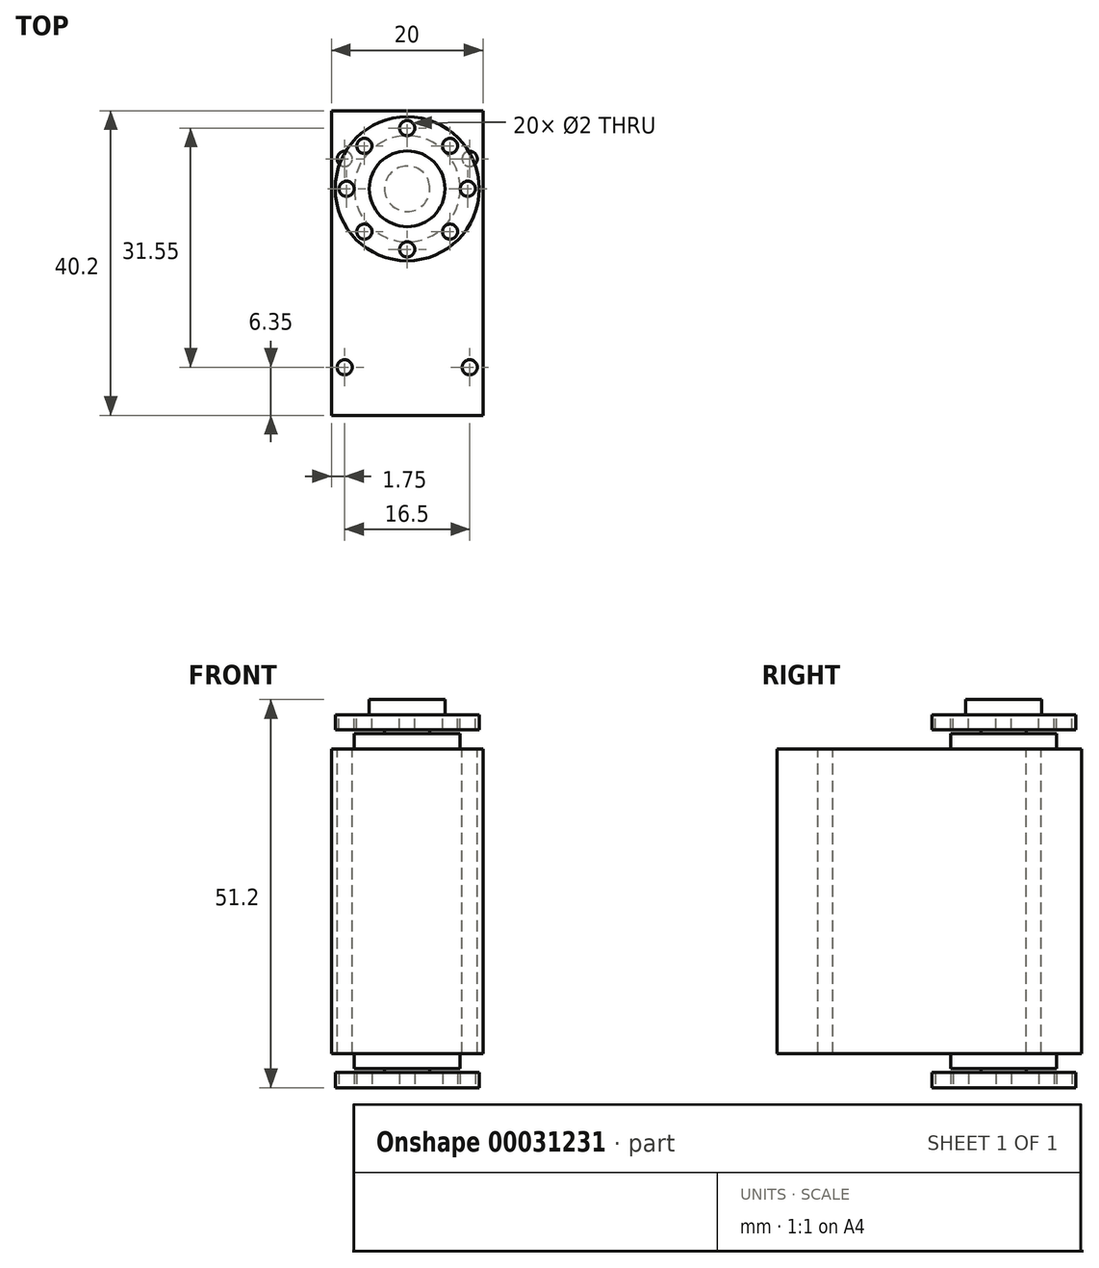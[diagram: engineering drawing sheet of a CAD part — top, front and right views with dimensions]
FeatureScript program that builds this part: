
annotation { "Feature Type Name" : "Feature", "Feature Type Description" : "" }
export const myFeature = defineFeature(function(context is Context, id is Id, definition is map)
    precondition{}
    {
        {
            var Q0;
            Q0=qCreatedBy(makeId("Top.planeOp"),FACE);
            var sketch = newSketch(context, id + "F0", { "sketchPlane" : qUnion([Q0])});
            skLineSegment(sketch, "E0.bottom", {"start": v(0, 0) * mm, "end": v(20, 0) * mm});
            skLineSegment(sketch, "E0.top", {"start": v(0, 40.2) * mm, "end": v(20, 40.2) * mm});
            skLineSegment(sketch, "E0.left", {"start": v(0, 0) * mm, "end": v(0, 40.2) * mm});
            skLineSegment(sketch, "E0.right", {"start": v(20, 0) * mm, "end": v(20, 40.2) * mm});
            skSolve(sketch);
        }
        {
            var Q0;
            Q0 = qSketchRegion(id + "F0", true);
            extrude(context, id + "F1", {"entities" : qUnion([Q0]), "depth" : 40.2 * mm});
        }
        {
            var Q0;
            Q0=makeQuery(id+"F1.opExtrude","CAP_FACE",FACE,{"disambiguationData":[OSD([sQuery(id+"F0.wireOp",EDGE,"E0.bottom"),sQuery(id+"F0.wireOp",EDGE,"E0.top"),sQuery(id+"F0.wireOp",EDGE,"E0.left"),sQuery(id+"F0.wireOp",EDGE,"E0.right")])],"isStart":false});
            var sketch = newSketch(context, id + "F2", { "sketchPlane" : qUnion([Q0])});
            skLineSegment(sketch, "E1", {"start": v(10, 40.2) * mm, "end": v(10, 0) * mm, "construction": true});
            skLineSegment(sketch, "E2", {"start": v(0, 20.1) * mm, "end": v(20, 20.1) * mm, "construction": true});
            skCircle(sketch, "E3", {"center": v(1.75, 33.85) * mm, "radius": 1 * mm});
            skCircle(sketch, "E4.MirrorC", {"center": v(18.25, 33.85) * mm, "radius": 1 * mm});
            skCircle(sketch, "E5.MirrorC", {"center": v(1.75, 6.35) * mm, "radius": 1 * mm});
            skCircle(sketch, "E6.MirrorC", {"center": v(18.25, 6.35) * mm, "radius": 1 * mm});
            skSolve(sketch);
        }
        {
            var Q0;
            Q0 = qSketchRegion(id + "F2", true);
            extrude(context, id + "F3", {"entities" : qUnion([Q0]), "operationType" : NewBodyOperationType.REMOVE, "endBound" : BoundingType.THROUGH_ALL, "oppositeDirection" : true, "depth" : 25 * mm});
        }
        {
            var Q0;
            Q0=makeQuery(id+"F1.opExtrude","CAP_FACE",FACE,{"disambiguationData":[OSD([sQuery(id+"F0.wireOp",EDGE,"E0.bottom"),sQuery(id+"F0.wireOp",EDGE,"E0.top"),sQuery(id+"F0.wireOp",EDGE,"E0.left"),sQuery(id+"F0.wireOp",EDGE,"E0.right")])],"isStart":false});
            var sketch = newSketch(context, id + "F4", { "sketchPlane" : qUnion([Q0])});
            skCircle(sketch, "E7", {"center": v(10, 29.9) * mm, "radius": 7 * mm});
            skLineSegment(sketch, "E8", {"start": v(0, 20.1) * mm, "end": v(20, 20.1) * mm, "construction": true});
            skSolve(sketch);
        }
        {
            var Q0;
            Q0 = qSketchRegion(id + "F4", true);
            extrude(context, id + "F5", {"entities" : qUnion([Q0]), "operationType" : NewBodyOperationType.ADD, "depth" : 2 * mm, "hasSecondDirection" : true, "secondDirectionOppositeDirection" : true, "secondDirectionDepth" : (40.2 + 2) * mm});
        }
        {
            var Q0;
            Q0=makeQuery(id+"F5.opExtrude","CAP_FACE",FACE,{"disambiguationData":[OSD([sQuery(id+"F4.wireOp",EDGE,"E7")])],"isStart":false});
            var sketch = newSketch(context, id + "F6", { "sketchPlane" : qUnion([Q0])});
            skCircle(sketch, "E9", {"center": v(10, 29.9) * mm, "radius": 3 * mm});
            skSolve(sketch);
        }
        {
            var Q0;
            Q0 = qSketchRegion(id + "F6", true);
            extrude(context, id + "F7", {"entities" : qUnion([Q0]), "operationType" : NewBodyOperationType.ADD, "depth" : 2.5 * mm});
        }
        {
            var Q0;
            Q0=makeQuery(id+"F7.opExtrude","CAP_FACE",FACE,{"disambiguationData":[OSD([sQuery(id+"F6.wireOp",EDGE,"E9")])],"isStart":false});
            var sketch = newSketch(context, id + "F8", { "sketchPlane" : qUnion([Q0])});
            skCircle(sketch, "E10", {"center": v(10, 29.9) * mm, "radius": 9.5 * mm});
            skCircle(sketch, "E11", {"center": v(10, 29.9) * mm, "radius": 8 * mm, "construction": true});
            skCircle(sketch, "E12", {"center": v(10, 37.9) * mm, "radius": 1 * mm});
            skCircle(sketch, "E13.1.0", {"center": v(4.34, 35.56) * mm, "radius": 1 * mm});
            skCircle(sketch, "E13.2.0", {"center": v(2, 29.9) * mm, "radius": 1 * mm});
            skCircle(sketch, "E13.3.0", {"center": v(4.34, 24.24) * mm, "radius": 1 * mm});
            skCircle(sketch, "E13.4.0", {"center": v(10, 21.9) * mm, "radius": 1 * mm});
            skCircle(sketch, "E13.5.0", {"center": v(15.66, 24.24) * mm, "radius": 1 * mm});
            skCircle(sketch, "E13.6.0", {"center": v(18, 29.9) * mm, "radius": 1 * mm});
            skCircle(sketch, "E13.7.0", {"center": v(15.66, 35.56) * mm, "radius": 1 * mm});
            skSolve(sketch);
        }
        {
            var Q0;
            Q0 = qSketchRegion(id + "F8", true);
            extrude(context, id + "F9", {"entities" : qUnion([Q0]), "operationType" : NewBodyOperationType.ADD, "oppositeDirection" : true, "depth" : 2 * mm});
        }
        {
            var Q0;
            Q0=qCreatedBy(makeId("Top.planeOp"),FACE);
            cPlane(context, id + "F10", {"entities" : qUnion([Q0]), "cplaneType" : CPlaneType.OFFSET, "offset" : (40.2 / 2) * mm, "width" : 150 * mm, "height" : 150 * mm});
        }
        {
            var Q0;
            Q0=makeQuery(id+"F9.opExtrude","SWEPT_BODY",BODY,{"disambiguationData":[OSD([sQuery(id+"F8.wireOp",EDGE,"E10"),sQuery(id+"F8.wireOp",EDGE,"E12"),sQuery(id+"F8.wireOp",EDGE,"E13.1.0"),sQuery(id+"F8.wireOp",EDGE,"E13.2.0"),sQuery(id+"F8.wireOp",EDGE,"E13.3.0"),sQuery(id+"F8.wireOp",EDGE,"E13.4.0"),sQuery(id+"F8.wireOp",EDGE,"E13.5.0"),sQuery(id+"F8.wireOp",EDGE,"E13.6.0"),sQuery(id+"F8.wireOp",EDGE,"E13.7.0")])]});
            var Q1;
            Q1=makeQuery(id+"F1.opExtrude","SWEPT_BODY",BODY,{"disambiguationData":[OSD([sQuery(id+"F0.wireOp",EDGE,"E0.bottom"),sQuery(id+"F0.wireOp",EDGE,"E0.top"),sQuery(id+"F0.wireOp",EDGE,"E0.left"),sQuery(id+"F0.wireOp",EDGE,"E0.right")])]});
            var Q2;
            Q2=qCreatedBy(id+"F10.planeOp",FACE);
            mirror(context, id + "F11", {"operationType" : NewBodyOperationType.ADD, "entities" : qUnion([Q0, Q1]), "mirrorPlane" : qUnion([Q2])});
        }
        {
            var Q0;
            Q0=makeQuery(id+"F9.boolean.opBoolean","MERGE",FACE,{"derivedFrom":[makeQuery(id+"F7.opExtrude","CAP_FACE",FACE,{"disambiguationData":[OSD([sQuery(id+"F6.wireOp",EDGE,"E9")])],"isStart":false}),makeQuery(id+"F9.opExtrude","CAP_FACE",FACE,{"disambiguationData":[OSD([sQuery(id+"F8.wireOp",EDGE,"E10"),sQuery(id+"F8.wireOp",EDGE,"E12"),sQuery(id+"F8.wireOp",EDGE,"E13.1.0"),sQuery(id+"F8.wireOp",EDGE,"E13.2.0"),sQuery(id+"F8.wireOp",EDGE,"E13.3.0"),sQuery(id+"F8.wireOp",EDGE,"E13.4.0"),sQuery(id+"F8.wireOp",EDGE,"E13.5.0"),sQuery(id+"F8.wireOp",EDGE,"E13.6.0"),sQuery(id+"F8.wireOp",EDGE,"E13.7.0")])],"isStart":true})]});
            var sketch = newSketch(context, id + "F12", { "sketchPlane" : qUnion([Q0])});
            skCircle(sketch, "E14", {"center": v(10, 29.9) * mm, "radius": 5 * mm});
            skSolve(sketch);
        }
        {
            var Q0;
            Q0 = qSketchRegion(id + "F12", true);
            extrude(context, id + "F13", {"entities" : qUnion([Q0]), "operationType" : NewBodyOperationType.ADD, "depth" : 2 * mm});
        }
    });
